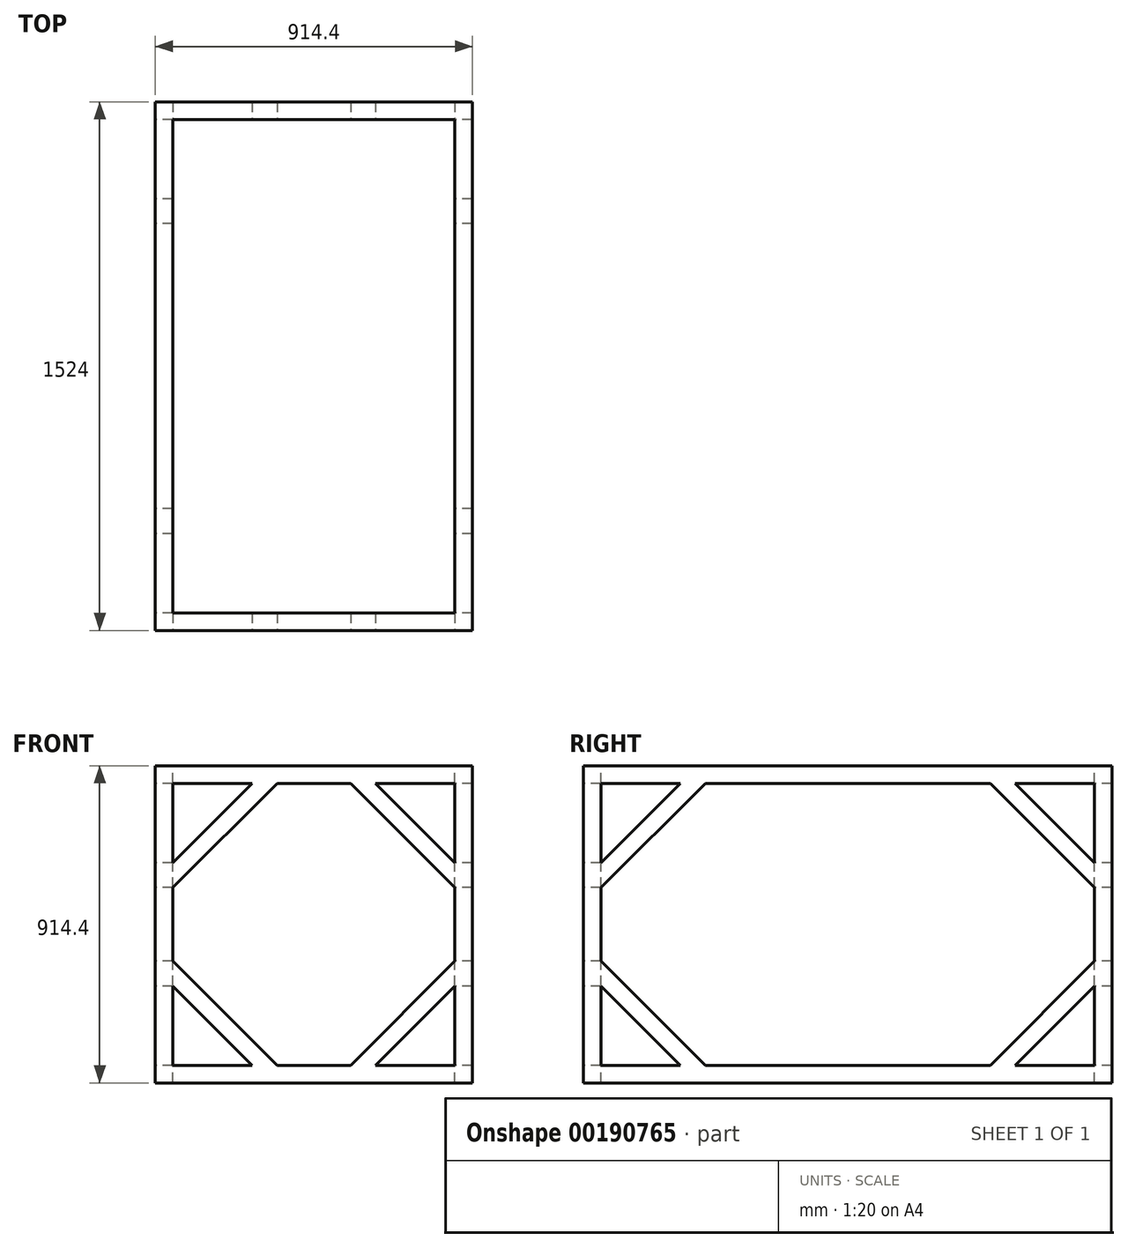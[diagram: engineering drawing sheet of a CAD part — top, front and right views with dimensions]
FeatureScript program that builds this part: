
annotation { "Feature Type Name" : "Feature", "Feature Type Description" : "" }
export const myFeature = defineFeature(function(context is Context, id is Id, definition is map)
    precondition{}
    {
        {
            var Q0;
            Q0=qCreatedBy(makeId("Top.planeOp"),FACE);
            var sketch = newSketch(context, id + "F0", { "sketchPlane" : qUnion([Q0])});
            skPoint(sketch, "E0.end.orphan", {"position": v(72.09, -83.35) * mm});
            skPoint(sketch, "E0.start.orphan", {"position": v(-65.3, -83.35) * mm});
            skLineSegment(sketch, "E1", {"start": v(0, 0) * mm, "end": v(914.4, 0) * mm});
            skLineSegment(sketch, "E2", {"start": v(914.4, 0) * mm, "end": v(914.4, 1524) * mm});
            skLineSegment(sketch, "E3", {"start": v(914.4, 1524) * mm, "end": v(0, 1524) * mm});
            skLineSegment(sketch, "E4", {"start": v(0, 1524) * mm, "end": v(0, 0) * mm});
            skSolve(sketch);
        }
        {
            var Q0;
            Q0 = qSketchRegion(id + "F0", true);
            extrude(context, id + "F1", {"entities" : qUnion([Q0]), "depth" : 914.4 * mm});
        }
        {
            var Q0;
            Q0=qCreatedBy(makeId("Right.planeOp"),FACE);
            var sketch = newSketch(context, id + "F2", { "sketchPlane" : qUnion([Q0])});
            skLineSegment(sketch, "E5", {"start": v(1473.2, 50.8) * mm, "end": v(1473.2, 863.6) * mm});
            skLineSegment(sketch, "E6", {"start": v(1473.2, 863.6) * mm, "end": v(50.8, 863.6) * mm});
            skLineSegment(sketch, "E7", {"start": v(50.8, 863.6) * mm, "end": v(50.8, 50.8) * mm});
            skLineSegment(sketch, "E8", {"start": v(50.8, 50.8) * mm, "end": v(1473.2, 50.8) * mm});
            skLineSegment(sketch, "E9", {"start": v(1473.2, 635) * mm, "end": v(1244.6, 863.6) * mm});
            skLineSegment(sketch, "E10", {"start": v(1473.2, 279.4) * mm, "end": v(1244.6, 50.8) * mm});
            skLineSegment(sketch, "E11", {"start": v(279.4, 863.6) * mm, "end": v(50.8, 635) * mm});
            skLineSegment(sketch, "E12", {"start": v(279.4, 50.8) * mm, "end": v(50.8, 279.4) * mm});
            skLineSegment(sketch, "E13", {"start": v(351.24, 863.6) * mm, "end": v(50.8, 563.16) * mm});
            skLineSegment(sketch, "E14", {"start": v(351.24, 50.8) * mm, "end": v(50.8, 351.24) * mm});
            skLineSegment(sketch, "E15", {"start": v(1473.2, 563.16) * mm, "end": v(1172.76, 863.6) * mm});
            skLineSegment(sketch, "E16", {"start": v(1172.76, 50.8) * mm, "end": v(1473.2, 351.24) * mm});
            skSolve(sketch);
        }
        {
            var Q0;
            {var subQ3=sQuery(id+"F2.wireOp",EDGE,"E9");Q0=makeQuery(id+"F2.imprint","IMPRINT",FACE,{"disambiguationData":[TD([[makeQuery(id+"F2.imprint","IMPRINT",EDGE,{"derivedFrom":subQ3}),-1.0]])]});}
            var Q1;
            {var subQ3=sQuery(id+"F2.wireOp",EDGE,"E10");Q1=makeQuery(id+"F2.imprint","IMPRINT",FACE,{"disambiguationData":[TD([[makeQuery(id+"F2.imprint","IMPRINT",EDGE,{"derivedFrom":subQ3}),1.0]])]});}
            var Q2;
            {var subQ3=sQuery(id+"F2.wireOp",EDGE,"E13");Q2=makeQuery(id+"F2.imprint","IMPRINT",FACE,{"disambiguationData":[TD([[makeQuery(id+"F2.imprint","IMPRINT",EDGE,{"derivedFrom":subQ3}),1.0]])]});}
            var Q3;
            {var subQ3=sQuery(id+"F2.wireOp",EDGE,"E11");Q3=makeQuery(id+"F2.imprint","IMPRINT",FACE,{"disambiguationData":[TD([[makeQuery(id+"F2.imprint","IMPRINT",EDGE,{"derivedFrom":subQ3}),-1.0]])]});}
            var Q4;
            {var subQ3=sQuery(id+"F2.wireOp",EDGE,"E12");Q4=makeQuery(id+"F2.imprint","IMPRINT",FACE,{"disambiguationData":[TD([[makeQuery(id+"F2.imprint","IMPRINT",EDGE,{"derivedFrom":subQ3}),1.0]])]});}
            extrude(context, id + "F3", {"entities" : qUnion([Q0, Q1, Q2, Q3, Q4]), "operationType" : NewBodyOperationType.REMOVE, "depth" : 2540 * mm});
        }
        {
            var Q0;
            Q0=qCreatedBy(makeId("Front.planeOp"),FACE);
            var sketch = newSketch(context, id + "F4", { "sketchPlane" : qUnion([Q0])});
            skLineSegment(sketch, "E17", {"start": v(50.8, 50.8) * mm, "end": v(863.6, 50.8) * mm});
            skLineSegment(sketch, "E18", {"start": v(863.6, 50.8) * mm, "end": v(863.6, 863.6) * mm});
            skLineSegment(sketch, "E19", {"start": v(863.6, 863.6) * mm, "end": v(50.8, 863.6) * mm});
            skLineSegment(sketch, "E20", {"start": v(50.8, 863.6) * mm, "end": v(50.8, 50.8) * mm});
            skPoint(sketch, "E21.orphan", {"position": v(46.94, 50.8) * mm});
            skLineSegment(sketch, "E22", {"start": v(50.8, 563.16) * mm, "end": v(351.24, 863.6) * mm});
            skLineSegment(sketch, "E23", {"start": v(50.8, 635) * mm, "end": v(279.4, 863.6) * mm});
            skLineSegment(sketch, "E24", {"start": v(50.8, 351.24) * mm, "end": v(351.24, 50.8) * mm});
            skLineSegment(sketch, "E25", {"start": v(50.8, 279.4) * mm, "end": v(279.4, 50.8) * mm});
            skLineSegment(sketch, "E26", {"start": v(635, 863.6) * mm, "end": v(863.6, 635) * mm});
            skLineSegment(sketch, "E27", {"start": v(563.16, 863.6) * mm, "end": v(863.6, 563.16) * mm});
            skLineSegment(sketch, "E28", {"start": v(635, 50.8) * mm, "end": v(863.6, 279.4) * mm});
            skLineSegment(sketch, "E29", {"start": v(563.16, 50.8) * mm, "end": v(863.6, 351.24) * mm});
            skSolve(sketch);
        }
        {
            var Q0;
            {var subQ0=sQuery(id+"F4.wireOp",EDGE,"E22");Q0=makeQuery(id+"F4.imprint","IMPRINT",FACE,{"disambiguationData":[TD([[makeQuery(id+"F4.imprint","IMPRINT",EDGE,{"derivedFrom":subQ0}),-1.0]])]});}
            var Q1;
            {var subQ3=sQuery(id+"F4.wireOp",EDGE,"E23");Q1=makeQuery(id+"F4.imprint","IMPRINT",FACE,{"disambiguationData":[TD([[makeQuery(id+"F4.imprint","IMPRINT",EDGE,{"derivedFrom":subQ3}),1.0]])]});}
            var Q2;
            {var subQ3=sQuery(id+"F4.wireOp",EDGE,"E25");Q2=makeQuery(id+"F4.imprint","IMPRINT",FACE,{"disambiguationData":[TD([[makeQuery(id+"F4.imprint","IMPRINT",EDGE,{"derivedFrom":subQ3}),-1.0]])]});}
            var Q3;
            {var subQ3=sQuery(id+"F4.wireOp",EDGE,"E28");Q3=makeQuery(id+"F4.imprint","IMPRINT",FACE,{"disambiguationData":[TD([[makeQuery(id+"F4.imprint","IMPRINT",EDGE,{"derivedFrom":subQ3}),-1.0]])]});}
            var Q4;
            {var subQ3=sQuery(id+"F4.wireOp",EDGE,"E26");Q4=makeQuery(id+"F4.imprint","IMPRINT",FACE,{"disambiguationData":[TD([[makeQuery(id+"F4.imprint","IMPRINT",EDGE,{"derivedFrom":subQ3}),1.0]])]});}
            extrude(context, id + "F5", {"entities" : qUnion([Q0, Q1, Q2, Q3, Q4]), "operationType" : NewBodyOperationType.REMOVE, "oppositeDirection" : true, "depth" : 2540 * mm});
        }
        {
            var Q0;
            Q0=makeQuery(id+"F1.opExtrude","CAP_FACE",FACE,{"disambiguationData":[OSD([sQuery(id+"F0.wireOp",EDGE,"E1"),sQuery(id+"F0.wireOp",EDGE,"E2"),sQuery(id+"F0.wireOp",EDGE,"E3"),sQuery(id+"F0.wireOp",EDGE,"E4")])],"isStart":false});
            var sketch = newSketch(context, id + "F6", { "sketchPlane" : qUnion([Q0])});
            skLineSegment(sketch, "E30", {"start": v(50.8, 1472.93) * mm, "end": v(50.8, 50.8) * mm});
            skLineSegment(sketch, "E31", {"start": v(50.8, 50.8) * mm, "end": v(863.6, 50.8) * mm});
            skLineSegment(sketch, "E32", {"start": v(863.6, 50.8) * mm, "end": v(863.6, 1473.2) * mm});
            skLineSegment(sketch, "E33", {"start": v(863.6, 1473.2) * mm, "end": v(50.8, 1473.2) * mm});
            skLineSegment(sketch, "E34", {"start": v(50.8, 1473.2) * mm, "end": v(50.8, 1472.93) * mm});
            skSolve(sketch);
        }
        {
            var Q0;
            Q0 = qSketchRegion(id + "F6", true);
            extrude(context, id + "F7", {"entities" : qUnion([Q0]), "operationType" : NewBodyOperationType.REMOVE, "oppositeDirection" : true, "depth" : 914.4 * mm});
        }
    });
